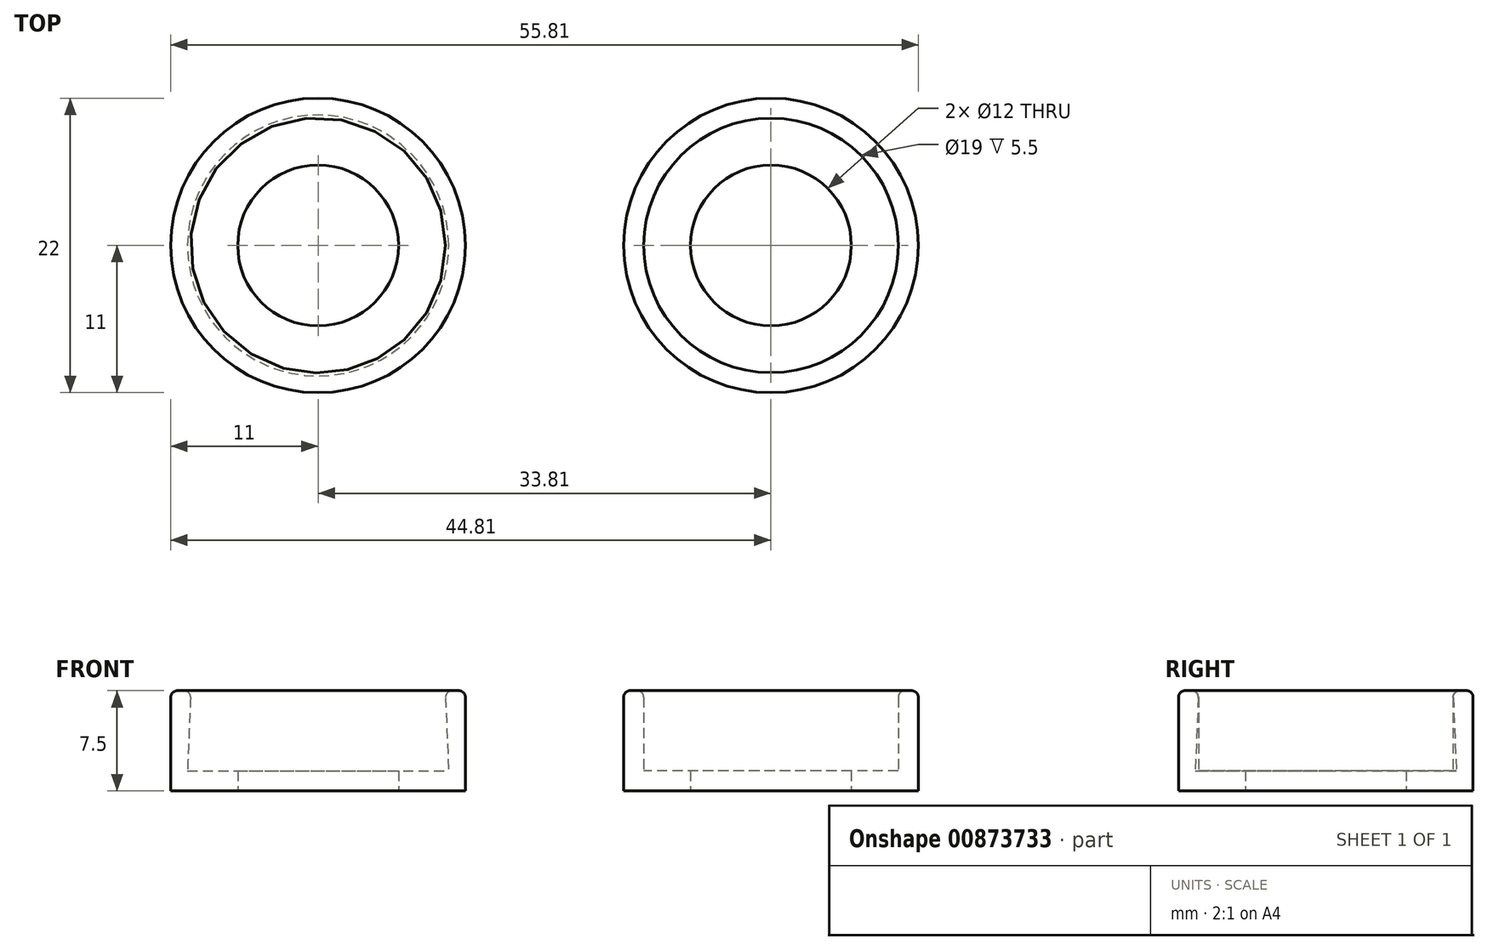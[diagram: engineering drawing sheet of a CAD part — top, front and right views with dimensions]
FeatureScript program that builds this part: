
annotation { "Feature Type Name" : "Feature", "Feature Type Description" : "" }
export const myFeature = defineFeature(function(context is Context, id is Id, definition is map)
    precondition{}
    {
        {
            var Q0;
            Q0=qCreatedBy(makeId("Top.planeOp"),FACE);
            var sketch = newSketch(context, id + "F0", { "sketchPlane" : qUnion([Q0])});
            skCircle(sketch, "E0", {"center": v(0, 0) * mm, "radius": 11 * mm});
            skCircle(sketch, "E1", {"center": v(0, 0) * mm, "radius": 9.5 * mm});
            skCircle(sketch, "E2", {"center": v(0, 0) * mm, "radius": 6 * mm});
            skSolve(sketch);
        }
        {
            var Q0;
            Q0=makeQuery(id+"F0.imprint","IMPRINT",FACE,{"disambiguationData":[TD([[makeQuery(id+"F0.imprint","IMPRINT",EDGE,{"derivedFrom":sQuery(id+"F0.wireOp",EDGE,"E0")}),1.0]])]});
            extrude(context, id + "F1", {"entities" : qUnion([Q0]), "depth" : 7.5 * mm, "offsetDistance" : 25 * mm});
        }
        {
            var Q0;
            Q0=makeQuery(id+"F0.imprint","IMPRINT",FACE,{"disambiguationData":[TD([[makeQuery(id+"F0.imprint","IMPRINT",EDGE,{"derivedFrom":sQuery(id+"F0.wireOp",EDGE,"E1")}),1.0]])]});
            extrude(context, id + "F2", {"entities" : qUnion([Q0]), "operationType" : NewBodyOperationType.ADD, "depth" : 1.5 * mm, "offsetDistance" : 25 * mm});
        }
        {
            var Q0;
            Q0=makeQuery(id+"F1.opExtrude","CAP_EDGE",EDGE,{"disambiguationData":[OSD([sQuery(id+"F0.wireOp",EDGE,"E0")])],"isStart":false});
            var Q1;
            Q1=makeQuery(id+"F1.opExtrude","CAP_EDGE",EDGE,{"disambiguationData":[OSD([sQuery(id+"F0.wireOp",EDGE,"E1")])],"isStart":false});
            fillet(context, id + "F3", {"entities" : qUnion([Q0, Q1]), "radius" : .5 * mm, "tangentPropagation" : true, "allowEdgeOverflow" : false});
        }
        {
            var Q0;
            Q0=qCreatedBy(makeId("Front.planeOp"),FACE);
            var sketch = newSketch(context, id + "F4", { "sketchPlane" : qUnion([Q0])});
            skLineSegment(sketch, "E3.bottom", {"start": v(-39.81, 1.5) * mm, "end": v(-44.81, 1.5) * mm});
            skLineSegment(sketch, "E3.top", {"start": v(-39.81, 0) * mm, "end": v(-44.81, 0) * mm});
            skLineSegment(sketch, "E3.left", {"start": v(-39.81, 1.5) * mm, "end": v(-39.81, 0) * mm});
            skLineSegment(sketch, "E3.right", {"start": v(-44.81, 1.5) * mm, "end": v(-44.81, 0) * mm});
            skLineSegment(sketch, "E4", {"start": v(-44.81, 1.5) * mm, "end": v(-44.81, 7.5) * mm});
            skLineSegment(sketch, "E5", {"start": v(-44.81, 7.5) * mm, "end": v(-43.31, 7.5) * mm});
            skPoint(sketch, "E6.endSnap0", {"position": v(-44.06, 7.5) * mm});
            skLineSegment(sketch, "E7", {"start": v(-43.31, 7.5) * mm, "end": v(-43.56, 1.5) * mm});
            skLineSegment(sketch, "E8", {"start": v(-39.81, 0) * mm, "end": v(-33.81, 0) * mm});
            skLineSegment(sketch, "E9", {"start": v(-33.81, 0) * mm, "end": v(-33.81, 7.5) * mm});
            skLineSegment(sketch, "E10", {"start": v(-43.56, 1.5) * mm, "end": v(-33.81, 1.5) * mm, "construction": true});
            skLineSegment(sketch, "E11", {"start": v(-43.31, 7.5) * mm, "end": v(-33.81, 7.5) * mm, "construction": true});
            skLineSegment(sketch, "E12", {"start": v(-39.81, 0) * mm, "end": v(-39.81, 0) * mm});
            skSolve(sketch);
        }
        {
            var Q0;
            {var subQ0=sQuery(id+"F4.wireOp",EDGE,"E4");Q0=makeQuery(id+"F4.imprint","IMPRINT",FACE,{"disambiguationData":[TD([[makeQuery(id+"F4.imprint","IMPRINT",EDGE,{"derivedFrom":subQ0}),-1.0]])]});}
            var Q1;
            Q1=makeQuery(id+"F4.imprint","IMPRINT",FACE,{"disambiguationData":[TD([[makeQuery(id+"F4.imprint","IMPRINT",EDGE,{"derivedFrom":sQuery(id+"F4.wireOp",EDGE,"E3.top")}),-1.0]])]});
            var Q2;
            Q2=sQuery(id+"F4.wireOp",EDGE,"E9");
            revolve(context, id + "F5", {"surfaceOperationType" : NewSurfaceOperationType.NEW, "entities" : qUnion([Q0, Q1]), "axis" : qUnion([Q2]), "revolveType" : RevolveType.FULL});
        }
        {
            var Q0;
            Q0=makeQuery(id+"F5.opRevolve","SWEPT_EDGE",EDGE,{"disambiguationData":[OSD([sQuery(id+"F4.wireOp",EDGE,"E4"),sQuery(id+"F4.wireOp",EDGE,"E5")])]});
            var Q1;
            Q1=makeQuery(id+"F5.opRevolve","SWEPT_EDGE",EDGE,{"disambiguationData":[OSD([sQuery(id+"F4.wireOp",EDGE,"E5"),sQuery(id+"F4.wireOp",EDGE,"E7")])]});
            fillet(context, id + "F6", {"entities" : qUnion([Q0, Q1]), "radius" : .5 * mm, "tangentPropagation" : true, "allowEdgeOverflow" : false});
        }
    });
